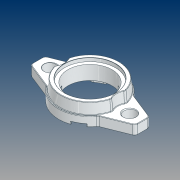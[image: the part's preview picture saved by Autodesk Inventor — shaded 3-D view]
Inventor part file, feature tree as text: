
AUTODESK INVENTOR PART (.ipt)
format: ipt  version: 2021 (Build 250183000, 183)  size: 911,872 bytes
history: native  units: mm
features: move_body x2, direct_edit x1, fillet x1
ambient origin geometry x8: Origin, YZ Plane, XZ Plane, XY Plane, X Axis, Y Axis, Z Axis, Center Point
bodies: Solid1 (feature_tree)
feature tree (4):
  direct_edit  "Direct Edit1"
  fillet  "Fillet7"  Radius=0.2mm
  move_body  "Move1"
  move_body  "Move2"
